# Revit family: Electronics_Touch-Panels_Biamp_Apprimo_Touch-10__
name_source: partatom
category: Communication Devices
units: mm (PartAtom-declared; Revit-internal decimal feet)

## family parameters
Cut with Voids When Loaded = No
Host = Face
Maintain Annotation Orientation = No
OmniClass Number = 23.85.10.17.11
OmniClass Title = Audio-Visual System Components
Part Type = Normal
Room Calculation Point = No
Round Connector Dimension = Use Diameter
Shared = No

## types (1)
- Touch 10
    Altitude = 0-6,600 ft (0-2000m) MSL
    Apparent Load = 0 VA
    Compliance = CE marked (Europe), RoHS Directive (Europe)
    Connector Description = PoE (IEEE 802.3at Class 3,15W)
    Controller Compatibility = Impera Alfa II, Impera Lima, Impera Tango, Impera Sierra II
    Default Elevation = 48 "
    Depth = 1.6 "
    Description = Apprimo Touch 10 Touch Panel
    Display Diagonal Size = 10 "
    Display Resolution = 1280x800
    Display Type = High-Contrast Capacitive Touch LCD
    Height = 6.67 "
    Housing Material = Biamp - Plastic - Black
    Humidity = 10-90% relative humidity (non-condensing)
    Included Accessories = Mounting bracket  and screws, Ejector Pin, USB-OTG adapter, Polishing cloth
    Manufacturer = Biamp
    Max Power Consumption = 0 W
    Maximum Display Brightness = 350 nits
    Mini USB port = USB 2.0
    Model = Apprimo Touch 10
    Network Connection = RJ-45 with Ethernet cable (Cat 5e and above)
    Number of Poles = 1
    Power Factor = 1
    Product Documentation Link = https://downloads.biamp.com
    Product Page URL = https://www.biamp.com
    Product data url = https://www.bimobject.com
    Sensors = Proximity; Ambient Light
    Table mount note = Optional tabletop stand accessory sold separately
    Temperature Range = 32 - 104° F (0 - 40° C)
    URL = https://www.biamp.com
    Voltage = 0 V
    Weight = 1.20 lbf
    Width = 9.7 "

## geometry (parser evidence)
native form markers: Sweep x7
no freeform markers — native parametric forms only
